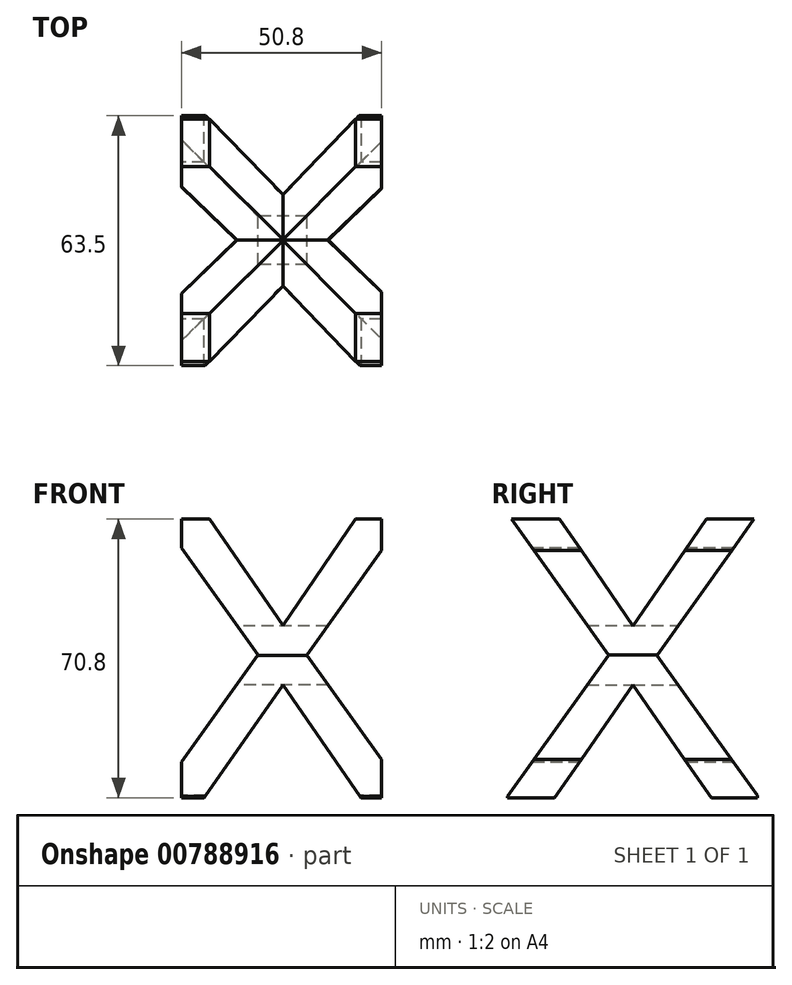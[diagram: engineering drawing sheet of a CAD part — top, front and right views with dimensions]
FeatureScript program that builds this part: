
annotation { "Feature Type Name" : "Feature", "Feature Type Description" : "" }
export const myFeature = defineFeature(function(context is Context, id is Id, definition is map)
    precondition{}
    {
        {
            var Q0;
            Q0=qCreatedBy(makeId("Front.planeOp"),FACE);
            var sketch = newSketch(context, id + "F0", { "sketchPlane" : qUnion([Q0])});
            skText(sketch, "E0", { "text": "x", "fontName": "OpenSans-Regular.ttf"});
            const initialGuessF0  = {"E0": [-0.03481, -0.03622, 1, 0, 0.09646]};
            skSetInitialGuess(sketch, initialGuessF0);
            skSolve(sketch);
        }
        {
            var Q0;
            Q0 = qSketchRegion(id + "F0", true);
            extrude(context, id + "F1", {"entities" : qUnion([Q0]), "depth" : 63.5 * mm, "offsetDistance" : 25.4 * mm});
        }
        {
            var Q0;
            Q0=qCreatedBy(makeId("Right.planeOp"),FACE);
            var sketch = newSketch(context, id + "F2", { "sketchPlane" : qUnion([Q0])});
            skText(sketch, "E1", { "text": "x", "fontName": "OpenSans-Regular.ttf"});
            const initialGuessF2  = {"E1": [-0.06625, -0.03581, 1, 0, 0.09525]};
            skSetInitialGuess(sketch, initialGuessF2);
            skSolve(sketch);
        }
        {
            var Q0;
            Q0 = qSketchRegion(id + "F2", true);
            extrude(context, id + "F3", {"entities" : qUnion([Q0]), "operationType" : NewBodyOperationType.INTERSECT, "depth" : 25.4 * mm, "offsetDistance" : 25.4 * mm, "hasSecondDirection" : true, "secondDirectionOppositeDirection" : true, "secondDirectionDepth" : 25.4 * mm});
        }
    });
